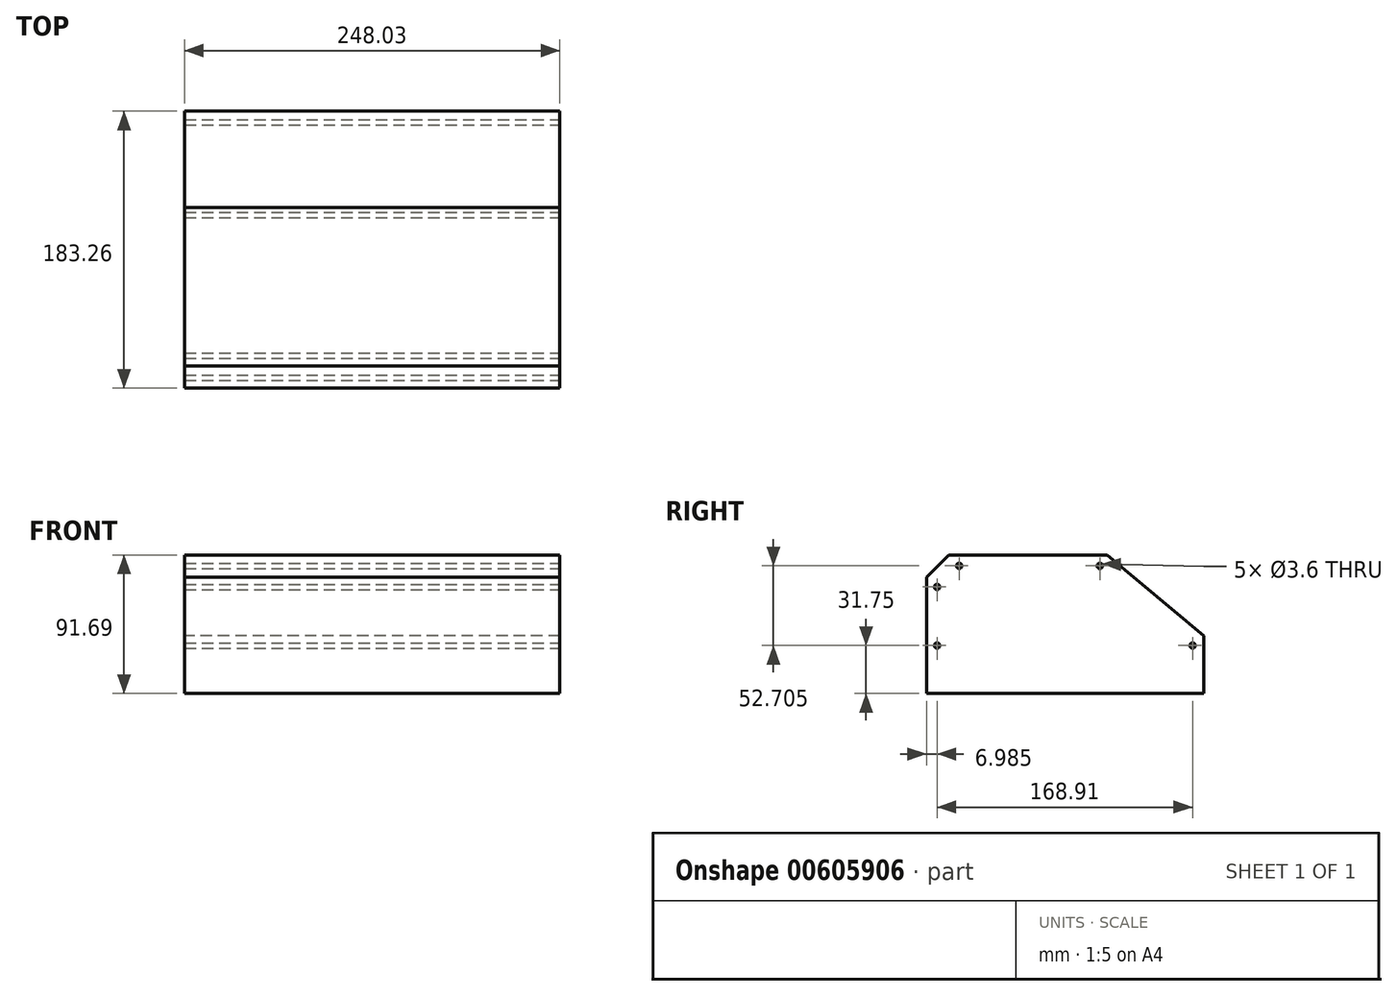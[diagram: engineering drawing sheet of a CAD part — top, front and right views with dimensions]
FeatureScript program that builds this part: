
annotation { "Feature Type Name" : "Feature", "Feature Type Description" : "" }
export const myFeature = defineFeature(function(context is Context, id is Id, definition is map)
    precondition{}
    {
        {
            var Q0;
            Q0=qCreatedBy(makeId("Right.planeOp"),FACE);
            var sketch = newSketch(context, id + "F0", { "sketchPlane" : qUnion([Q0])});
            skLineSegment(sketch, "E0", {"start": v(0, 0) * mm, "end": v(0, 76.88) * mm});
            skLineSegment(sketch, "E1", {"start": v(0, 76.88) * mm, "end": v(14.82, 91.7) * mm});
            skLineSegment(sketch, "E2", {"start": v(14.82, 91.7) * mm, "end": v(119.6, 91.7) * mm});
            skLineSegment(sketch, "E3", {"start": v(119.6, 91.7) * mm, "end": v(183.26, 38.1) * mm});
            skLineSegment(sketch, "E4", {"start": v(183.26, 38.1) * mm, "end": v(183.26, 0) * mm});
            skLineSegment(sketch, "E5", {"start": v(183.26, 0) * mm, "end": v(0, 0) * mm});
            skSolve(sketch);
        }
        {
            var Q0;
            Q0=qSketchRegion(id+"F0",true);
            extrude(context, id + "F1", {"entities" : qUnion([Q0]), "depth" : 248.03 * mm, "offsetDistance" : 25.4 * mm});
        }
        {
            var Q0;
            Q0=makeQuery(id+"F1.opExtrude","CAP_FACE",FACE,{"disambiguationData":[OSD([sQuery(id+"F0.wireOp",EDGE,"E0"),sQuery(id+"F0.wireOp",EDGE,"E1"),sQuery(id+"F0.wireOp",EDGE,"E2"),sQuery(id+"F0.wireOp",EDGE,"E3"),sQuery(id+"F0.wireOp",EDGE,"E4"),sQuery(id+"F0.wireOp",EDGE,"E5")])],"isStart":false});
            var sketch = newSketch(context, id + "F2", { "sketchPlane" : qUnion([Q0])});
            skPoint(sketch, "E6", {"position": v(6.99, 31.75) * mm});
            skPoint(sketch, "E7", {"position": v(6.98, 70.48) * mm});
            skPoint(sketch, "E8", {"position": v(21.59, 84.46) * mm});
            skPoint(sketch, "E9", {"position": v(114.55, 84.46) * mm});
            skPoint(sketch, "E10", {"position": v(175.9, 31.75) * mm});
            skSolve(sketch);
        }
        {
            var Q0;
            Q0=sQuery(id+"F2.wireOp",VERTEX,"E8");
            var Q1;
            Q1=sQuery(id+"F2.wireOp",VERTEX,"E7");
            var Q2;
            Q2=sQuery(id+"F2.wireOp",VERTEX,"E6");
            var Q3;
            Q3=sQuery(id+"F2.wireOp",VERTEX,"E10");
            var Q4;
            Q4=sQuery(id+"F2.wireOp",VERTEX,"E9");
            var Q5;
            Q5=makeQuery(id+"F1.opExtrude","SWEPT_BODY",BODY,{"disambiguationData":[OSD([sQuery(id+"F0.wireOp",EDGE,"E0"),sQuery(id+"F0.wireOp",EDGE,"E1"),sQuery(id+"F0.wireOp",EDGE,"E2"),sQuery(id+"F0.wireOp",EDGE,"E3"),sQuery(id+"F0.wireOp",EDGE,"E4"),sQuery(id+"F0.wireOp",EDGE,"E5")])]});
            hole(context, id + "F3", {"style" : HoleStyle.SIMPLE, "endStyle" : HoleEndStyle.THROUGH, "standardTappedOrClearance" : lookupTablePath({ "fit" : "Loose", "standard" : "ISO", "size" : "M3", "type" : "Clearance" }), "standardBlindInLast" : lookupTablePath({ "fit" : "Loose", "standard" : "ISO", "engagement" : "75%", "pitch" : "0.5 mm", "size" : "M3", "type" : "Clearance & tapped" }), "holeDiameter" : 3.6 * mm, "majorDiameter" : 5 * mm, "isTappedThrough" : true, "tappedDepth" : 19.05 * mm, "tapClearance" : 3, "startFromSketch" : true, "locations" : qUnion([Q0, Q1, Q2, Q3, Q4]), "scope" : qUnion([Q5])});
        }
    });
